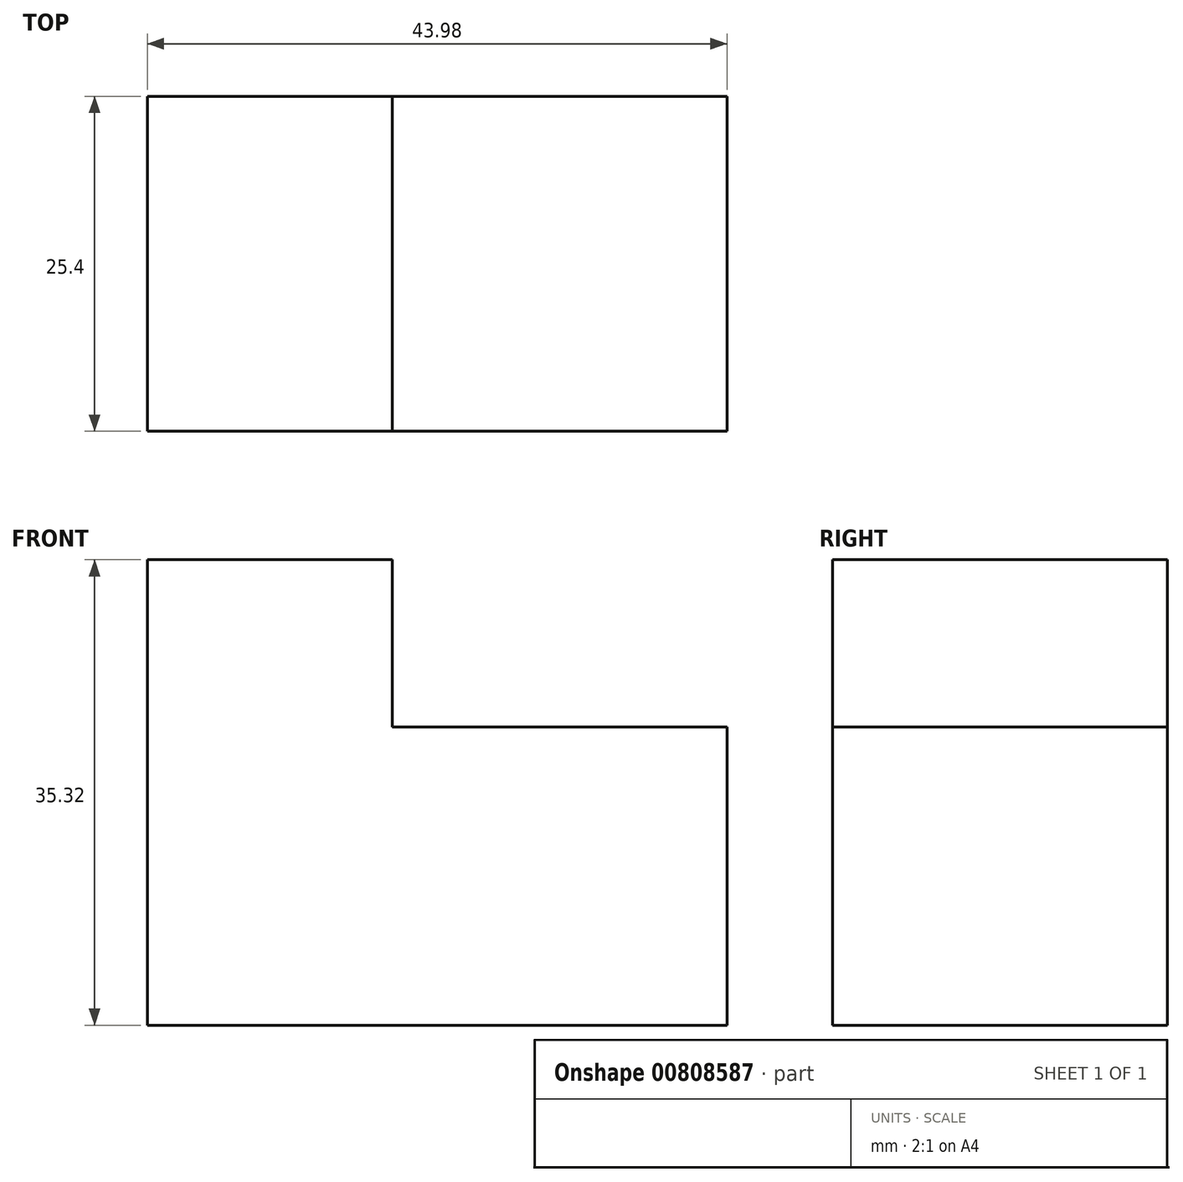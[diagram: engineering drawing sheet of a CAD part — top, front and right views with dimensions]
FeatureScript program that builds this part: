
annotation { "Feature Type Name" : "Feature", "Feature Type Description" : "" }
export const myFeature = defineFeature(function(context is Context, id is Id, definition is map)
    precondition{}
    {
        {
            var Q0;
            Q0=qCreatedBy(makeId("Front.planeOp"),FACE);
            var sketch = newSketch(context, id + "F0", { "sketchPlane" : qUnion([Q0])});
            skLineSegment(sketch, "E0", {"start": v(0, 0) * mm, "end": v(0, 35.32) * mm});
            skLineSegment(sketch, "E1", {"start": v(0, 35.32) * mm, "end": v(18.58, 35.32) * mm});
            skLineSegment(sketch, "E2", {"start": v(18.58, 35.32) * mm, "end": v(18.58, 22.62) * mm});
            skLineSegment(sketch, "E3", {"start": v(18.58, 22.62) * mm, "end": v(43.98, 22.62) * mm});
            skLineSegment(sketch, "E4", {"start": v(43.98, 22.62) * mm, "end": v(43.98, 0) * mm});
            skLineSegment(sketch, "E5", {"start": v(43.98, 0) * mm, "end": v(0, 0) * mm});
            skSolve(sketch);
        }
        {
            var Q0;
            Q0=makeQuery(id+"F0.imprint","IMPRINT",FACE,{"disambiguationData":[TD([[makeQuery(id+"F0.imprint","IMPRINT",EDGE,{"derivedFrom":sQuery(id+"F0.wireOp",EDGE,"E0")}),-1.0]])]});
            extrude(context, id + "F1", {"entities" : qUnion([Q0]), "depth" : 25.4 * mm, "offsetDistance" : 25.4 * mm});
        }
    });
